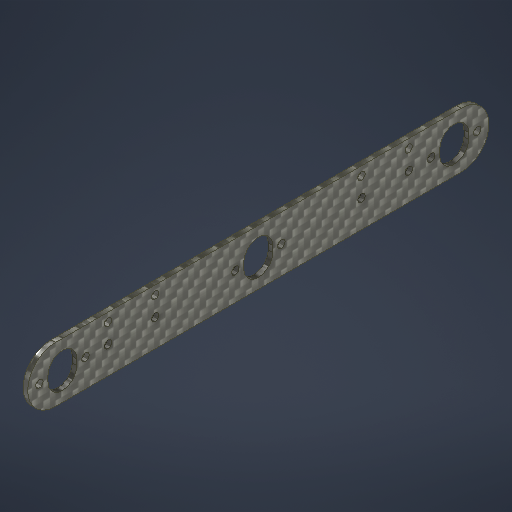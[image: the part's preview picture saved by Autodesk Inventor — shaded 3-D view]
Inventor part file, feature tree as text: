
AUTODESK INVENTOR PART (.ipt)
format: ipt  version: 2025 (Build 290162010, 162A)  size: 323,584 bytes
history: native  units: mm
features: extrude x1, sketch x1
ambient origin geometry x8: Origin, YZ Plane, XZ Plane, XY Plane, X Axis, Y Axis, Z Axis, Center Point
bodies: Solid1 (feature_tree)
feature tree (2):
  extrude  "Extrusion1"  Depth=2.0mm
  sketch  "Sketch1"  dims[d0=2.0mm d1=0.0mm d2=3.2mm d3=3.2mm d4=3.2mm d5=3.2mm d6=8.347mm d7=8.347mm d8=8.347mm d9=3.2mm d10=3.2mm d11=3.2mm d12=3.2mm d15=3.2mm d16=3.2mm d17=3.2mm d18=3.2mm d19=3.2mm d20=3.2mm]
